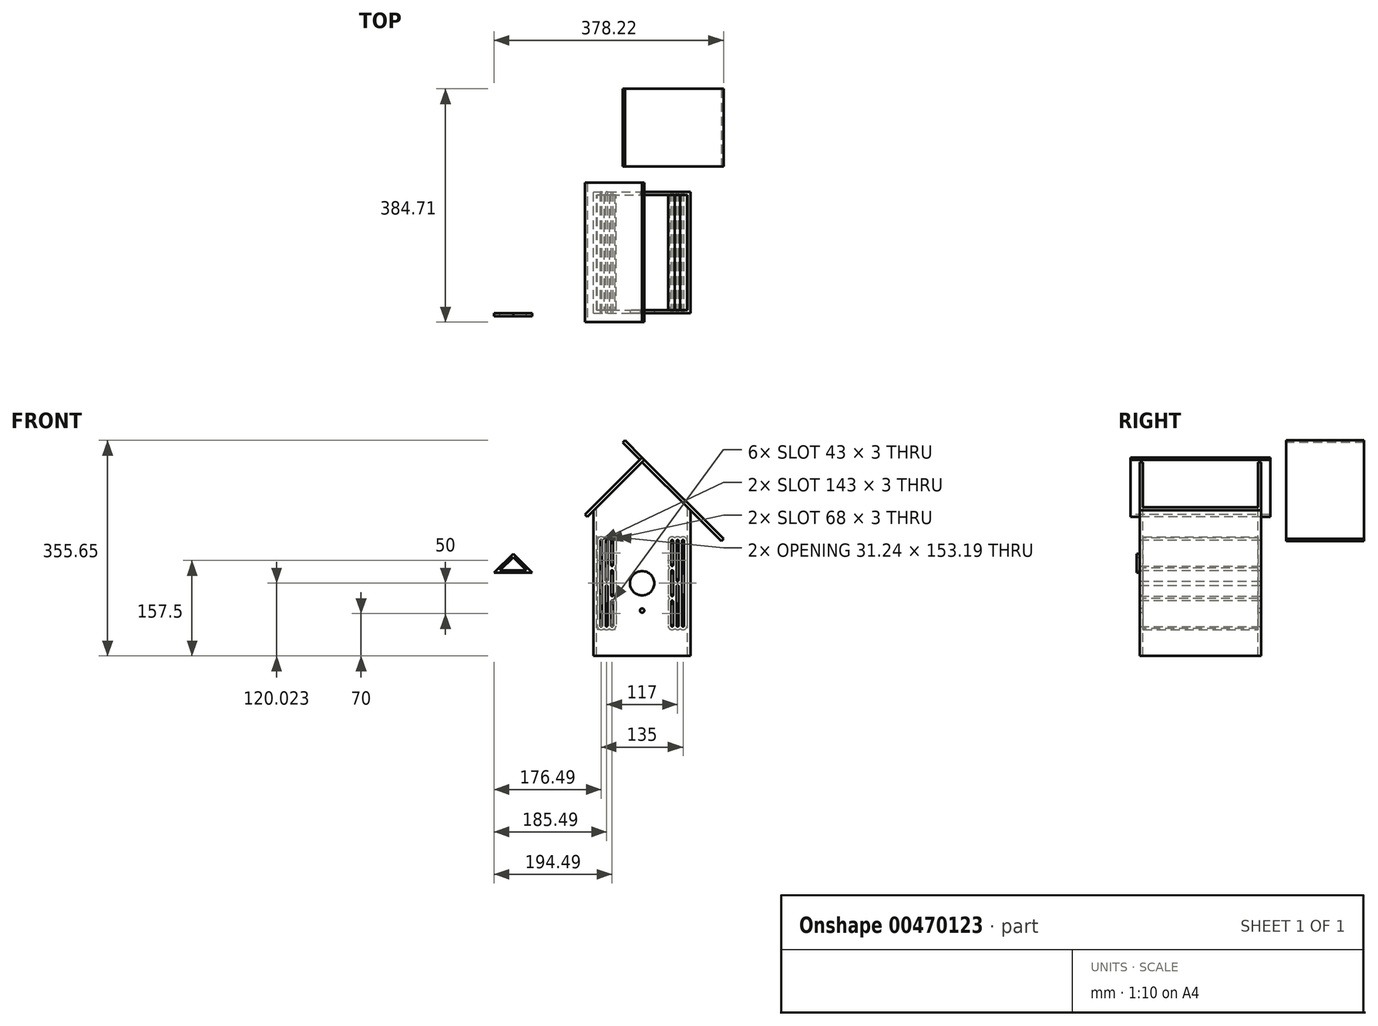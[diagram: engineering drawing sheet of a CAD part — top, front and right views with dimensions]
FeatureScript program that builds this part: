
annotation { "Feature Type Name" : "Feature", "Feature Type Description" : "" }
export const myFeature = defineFeature(function(context is Context, id is Id, definition is map)
    precondition{}
    {
        {
            var Q0;
            Q0=qCreatedBy(makeId("Front.planeOp"),FACE);
            var sketch = newSketch(context, id + "F0", { "sketchPlane" : qUnion([Q0])});
            skLineSegment(sketch, "E0.bottom", {"start": v(0, 0) * mm, "end": v(160, 0) * mm});
            skLineSegment(sketch, "E0.left", {"start": v(0, 0) * mm, "end": v(0, 240) * mm});
            skLineSegment(sketch, "E0.right", {"start": v(160, 0) * mm, "end": v(160, 240) * mm});
            skLineSegment(sketch, "E1", {"start": v(0, 240) * mm, "end": v(80, 320) * mm});
            skLineSegment(sketch, "E2", {"start": v(160, 240) * mm, "end": v(80, 320) * mm});
            skLineSegment(sketch, "E3", {"start": v(0, 240) * mm, "end": v(160, 240) * mm, "construction": true});
            skLineSegment(sketch, "E4.left", {"start": v(20, 190) * mm, "end": v(20, 125) * mm});
            skLineSegment(sketch, "E4.right", {"start": v(23, 190) * mm, "end": v(23, 125) * mm});
            skLineSegment(sketch, "E5", {"start": v(80, 249.53) * mm, "end": v(80, -21.44) * mm, "construction": true});
            skArc(sketch, "E6", {"start": v(23, 190) * mm, "mid": v(21.5, 191.5) * mm, "end": v(20, 190) * mm});
            skLineSegment(sketch, "E7", {"start": v(17, 266.29) * mm, "end": v(17, -25.67) * mm, "construction": true});
            skArc(sketch, "E8.MirrorCS", {"start": v(14, 50) * mm, "mid": v(12.5, 48.5) * mm, "end": v(11, 50) * mm});
            skArc(sketch, "E9.MirrorCS", {"start": v(11, 190) * mm, "mid": v(12.5, 191.5) * mm, "end": v(14, 190) * mm});
            skLineSegment(sketch, "E10.MirrorCS", {"start": v(11, 190) * mm, "end": v(11, 50) * mm});
            skLineSegment(sketch, "E11.MirrorCS", {"start": v(14, 190) * mm, "end": v(14, 50) * mm});
            skArc(sketch, "E12.MirrorCS", {"start": v(149, 190) * mm, "mid": v(147.5, 191.5) * mm, "end": v(146, 190) * mm});
            skArc(sketch, "E13.MirrorCS", {"start": v(146, 50) * mm, "mid": v(147.5, 48.5) * mm, "end": v(149, 50) * mm});
            skLineSegment(sketch, "E14.MirrorCS", {"start": v(149, 190) * mm, "end": v(149, 50) * mm});
            skLineSegment(sketch, "E15.MirrorCS", {"start": v(146, 190) * mm, "end": v(146, 50) * mm});
            skLineSegment(sketch, "E16.left", {"start": v(29, 190) * mm, "end": v(29, 150) * mm});
            skLineSegment(sketch, "E16.right", {"start": v(32, 190) * mm, "end": v(32, 150) * mm});
            skArc(sketch, "E17", {"start": v(29, 150) * mm, "mid": v(30.5, 148.5) * mm, "end": v(32, 150) * mm});
            skArc(sketch, "E18", {"start": v(32, 190) * mm, "mid": v(30.5, 191.5) * mm, "end": v(29, 190) * mm});
            skLineSegment(sketch, "E19.left", {"start": v(29, 140) * mm, "end": v(29, 100) * mm});
            skArc(sketch, "E20", {"start": v(32, 140) * mm, "mid": v(30.5, 141.5) * mm, "end": v(29, 140) * mm});
            skPoint(sketch, "E21.center.orphan", {"position": v(30.5, 70) * mm});
            skPoint(sketch, "E19.right.end.orphan", {"position": v(32, 40) * mm});
            skLineSegment(sketch, "E22", {"start": v(32, 140) * mm, "end": v(32, 100) * mm});
            skArc(sketch, "E23", {"start": v(29, 100) * mm, "mid": v(30.5, 98.5) * mm, "end": v(32, 100) * mm});
            skLineSegment(sketch, "E24", {"start": v(29, 90) * mm, "end": v(29, 50) * mm});
            skLineSegment(sketch, "E25", {"start": v(32, 90) * mm, "end": v(32, 50) * mm});
            skArc(sketch, "E26", {"start": v(29, 90) * mm, "mid": v(30.5, 91.5) * mm, "end": v(32, 90) * mm});
            skArc(sketch, "E27", {"start": v(29, 50) * mm, "mid": v(30.5, 48.5) * mm, "end": v(32, 50) * mm});
            skArc(sketch, "E28.MirrorCS", {"start": v(128, 190) * mm, "mid": v(129.5, 191.5) * mm, "end": v(131, 190) * mm});
            skArc(sketch, "E29.MirrorCS", {"start": v(128, 140) * mm, "mid": v(129.5, 141.5) * mm, "end": v(131, 140) * mm});
            skArc(sketch, "E30.MirrorCS", {"start": v(131, 150) * mm, "mid": v(129.5, 148.5) * mm, "end": v(128, 150) * mm});
            skArc(sketch, "E31.MirrorCS", {"start": v(131, 100) * mm, "mid": v(129.5, 98.5) * mm, "end": v(128, 100) * mm});
            skArc(sketch, "E32.MirrorCS", {"start": v(131, 90) * mm, "mid": v(129.5, 91.5) * mm, "end": v(128, 90) * mm});
            skArc(sketch, "E33.MirrorCS", {"start": v(131, 50) * mm, "mid": v(129.5, 48.5) * mm, "end": v(128, 50) * mm});
            skLineSegment(sketch, "E34.MirrorCS", {"start": v(131, 140) * mm, "end": v(131, 100) * mm});
            skLineSegment(sketch, "E35.MirrorCS", {"start": v(128, 90) * mm, "end": v(128, 50) * mm});
            skLineSegment(sketch, "E36.MirrorCS", {"start": v(131, 190) * mm, "end": v(131, 150) * mm});
            skLineSegment(sketch, "E37.MirrorCS", {"start": v(131, 90) * mm, "end": v(131, 50) * mm});
            skLineSegment(sketch, "E38.MirrorCS", {"start": v(128, 140) * mm, "end": v(128, 100) * mm});
            skLineSegment(sketch, "E39.MirrorCS", {"start": v(128, 190) * mm, "end": v(128, 150) * mm});
            skPoint(sketch, "E40.MirrorP", {"position": v(129.5, 70) * mm});
            skLineSegment(sketch, "E41", {"start": v(20.02, 115) * mm, "end": v(20.02, 50.05) * mm});
            skLineSegment(sketch, "E42", {"start": v(23.02, 115) * mm, "end": v(23.02, 50.05) * mm});
            skArc(sketch, "E43", {"start": v(23.02, 115) * mm, "mid": v(21.52, 116.5) * mm, "end": v(20.02, 115) * mm});
            skArc(sketch, "E44", {"start": v(20.02, 50.05) * mm, "mid": v(21.52, 48.55) * mm, "end": v(23.02, 50.05) * mm});
            skArc(sketch, "E45.MirrorCS", {"start": v(137, 190) * mm, "mid": v(138.5, 191.5) * mm, "end": v(140, 190) * mm});
            skArc(sketch, "E46.MirrorCS", {"start": v(136.98, 115) * mm, "mid": v(138.48, 116.5) * mm, "end": v(139.98, 115) * mm});
            skArc(sketch, "E47.MirrorCS", {"start": v(139.98, 50.05) * mm, "mid": v(138.48, 48.55) * mm, "end": v(136.98, 50.05) * mm});
            skLineSegment(sketch, "E48.MirrorCS", {"start": v(140, 190) * mm, "end": v(140, 125) * mm});
            skLineSegment(sketch, "E49.MirrorCS", {"start": v(139.98, 115) * mm, "end": v(139.98, 50.05) * mm});
            skLineSegment(sketch, "E50.MirrorCS", {"start": v(143, 266.29) * mm, "end": v(143, -25.67) * mm, "construction": true});
            skLineSegment(sketch, "E51.MirrorCS", {"start": v(137, 190) * mm, "end": v(137, 125) * mm});
            skLineSegment(sketch, "E52.MirrorCS", {"start": v(136.98, 115) * mm, "end": v(136.98, 50.05) * mm});
            skArc(sketch, "E53", {"start": v(20, 125) * mm, "mid": v(21.5, 123.5) * mm, "end": v(23, 125) * mm});
            skArc(sketch, "E54", {"start": v(137, 125) * mm, "mid": v(138.5, 123.5) * mm, "end": v(140, 125) * mm});
            skSolve(sketch);
        }
        {
            var Q0;
            Q0 = qSketchRegion(id + "F0", true);
            extrude(context, id + "F1", {"entities" : qUnion([Q0]), "offsetDistance" : 25 * mm, "depth" : 200 * mm});
        }
        {
            var Q0;
            Q0=makeQuery(id+"F1.opExtrude","SWEPT_FACE",FACE,{"disambiguationData":[OSD([sQuery(id+"F0.wireOp",EDGE,"E0.bottom")])]});
            var Q1;
            Q1=makeQuery(id+"F1.opExtrude","SWEPT_FACE",FACE,{"disambiguationData":[OSD([sQuery(id+"F0.wireOp",EDGE,"E2")])]});
            var Q2;
            Q2=makeQuery(id+"F1.opExtrude","SWEPT_FACE",FACE,{"disambiguationData":[OSD([sQuery(id+"F0.wireOp",EDGE,"E1")])]});
            shell(context, id + "F2", {"entities" : qUnion([Q0, Q1, Q2]), "thickness" : 5.12 * mm});
        }
        {
            var Q0;
            Q0=makeQuery(id+"F1.opExtrude","CAP_FACE",FACE,{"disambiguationData":[OSD([sQuery(id+"F0.wireOp",EDGE,"E0.bottom"),sQuery(id+"F0.wireOp",EDGE,"E0.left"),sQuery(id+"F0.wireOp",EDGE,"E0.right"),sQuery(id+"F0.wireOp",EDGE,"E1"),sQuery(id+"F0.wireOp",EDGE,"E2")])],"isStart":false});
            var sketch = newSketch(context, id + "F3", { "sketchPlane" : qUnion([Q0])});
            skLineSegment(sketch, "E55", {"start": v(80, 224.17) * mm, "end": v(80, 53.63) * mm, "construction": true});
            skLineSegment(sketch, "E56", {"start": v(0, 120) * mm, "end": v(241.44, 120) * mm, "construction": true});
            skLineSegment(sketch, "E57", {"start": v(17.26, 75) * mm, "end": v(140.48, 75) * mm, "construction": true});
            skCircle(sketch, "E58", {"center": v(80, 120) * mm, "radius": 20 * mm});
            skCircle(sketch, "E59", {"center": v(80, 75) * mm, "radius": 3.5 * mm});
            skSolve(sketch);
        }
        {
            var Q0;
            Q0=makeQuery(id+"F3.imprint","IMPRINT",FACE,{"disambiguationData":[TD([[makeQuery(id+"F3.imprint","IMPRINT",EDGE,{"derivedFrom":sQuery(id+"F3.wireOp",EDGE,"E58")}),1.0]])]});
            extrude(context, id + "F4", {"entities" : qUnion([Q0]), "operationType" : NewBodyOperationType.REMOVE, "oppositeDirection" : true, "depth" : 25 * mm, "offsetDistance" : 25 * mm});
        }
        {
            var Q0;
            Q0=makeQuery(id+"F3.imprint","IMPRINT",FACE,{"disambiguationData":[TD([[makeQuery(id+"F3.imprint","IMPRINT",EDGE,{"derivedFrom":sQuery(id+"F3.wireOp",EDGE,"E59")}),1.0]])]});
            var Q1;
            Q1=sQuery(id+"F3.wireOp",EDGE,"E59");
            extrude(context, id + "F5", {"entities" : qUnion([Q0]), "operationType" : NewBodyOperationType.REMOVE, "surfaceEntities" : qUnion([Q1]), "oppositeDirection" : true, "depth" : 220 * mm, "offsetDistance" : 25 * mm});
        }
        {
            var Q0;
            {var subQ0=sQuery(id+"F0.wireOp",EDGE,"E2");Q0=makeQuery(id+"F2.opShell","OFFSET_EDGE",EDGE,{"disambiguationData":[OSD([subQ0]),TDD([makeQuery(id+"F1.opExtrude","CAP_EDGE",EDGE,{"disambiguationData":[OSD([subQ0])],"isStart":false})])]});}
            var Q1;
            Q1=makeQuery(id+"F2.opShell","OFFSET_EDGE",EDGE,{"disambiguationData":[OSD([sQuery(id+"F0.wireOp",EDGE,"E0.right"),sQuery(id+"F0.wireOp",EDGE,"E2")])]});
            cPlane(context, id + "F6", {"entities" : qUnion([Q0, Q1]), "cplaneType" : CPlaneType.LINE_ANGLE, "offset" : 25 * mm, "angle" : 0 * degree, "width" : 150 * mm, "height" : 150 * mm});
        }
        {
            var Q0;
            Q0=qCreatedBy(id+"F6.planeOp",FACE);
            var sketch = newSketch(context, id + "F7", { "sketchPlane" : qUnion([Q0])});
            skLineSegment(sketch, "E60", {"start": v(-169.7, 215) * mm, "end": v(-41.57, 215) * mm});
            skLineSegment(sketch, "E61", {"start": v(-169.7, -15) * mm, "end": v(-41.57, -15) * mm});
            skLineSegment(sketch, "E62", {"start": v(-41.57, 215) * mm, "end": v(-41.57, -15) * mm});
            skLineSegment(sketch, "E63", {"start": v(-169.7, 215) * mm, "end": v(-169.7, -15) * mm});
            skSolve(sketch);
        }
        {
            var Q0;
            Q0 = qSketchRegion(id + "F7", true);
            extrude(context, id + "F8", {"entities" : qUnion([Q0]), "oppositeDirection" : true, "depth" : 5.12 * mm});
        }
        {
            var Q0;
            {var subQ0=sQuery(id+"F0.wireOp",EDGE,"E1");Q0=makeQuery(id+"F2.opShell","OFFSET_EDGE",EDGE,{"disambiguationData":[OSD([subQ0]),TDD([makeQuery(id+"F1.opExtrude","CAP_EDGE",EDGE,{"disambiguationData":[OSD([subQ0])],"isStart":false})])]});}
            var Q1;
            Q1=makeQuery(id+"F2.opShell","OFFSET_EDGE",EDGE,{"disambiguationData":[OSD([sQuery(id+"F0.wireOp",EDGE,"E0.left"),sQuery(id+"F0.wireOp",EDGE,"E1")])]});
            cPlane(context, id + "F9", {"entities" : qUnion([Q0, Q1]), "cplaneType" : CPlaneType.LINE_ANGLE, "offset" : 25 * mm, "angle" : 0 * degree, "width" : 150 * mm, "height" : 150 * mm});
        }
        {
            var Q0;
            Q0=qCreatedBy(id+"F9.planeOp",FACE);
            var sketch = newSketch(context, id + "F10", { "sketchPlane" : qUnion([Q0])});
            skLineSegment(sketch, "E64", {"start": v(-15, 287.96) * mm, "end": v(-15, 154.7) * mm});
            skLineSegment(sketch, "E65", {"start": v(215, 287.96) * mm, "end": v(215, 154.7) * mm});
            skLineSegment(sketch, "E66", {"start": v(-15, 287.96) * mm, "end": v(215, 287.96) * mm});
            skLineSegment(sketch, "E67", {"start": v(-15, 154.7) * mm, "end": v(215, 154.7) * mm});
            skSolve(sketch);
        }
        {
            var Q0;
            Q0 = qSketchRegion(id + "F10", true);
            extrude(context, id + "F11", {"entities" : qUnion([Q0]), "depth" : 5.12 * mm});
        }
        {
            var Q0;
            Q0=makeQuery(id+"F1.opExtrude","CAP_FACE",FACE,{"disambiguationData":[OSD([sQuery(id+"F0.wireOp",EDGE,"E0.bottom"),sQuery(id+"F0.wireOp",EDGE,"E0.left"),sQuery(id+"F0.wireOp",EDGE,"E0.right"),sQuery(id+"F0.wireOp",EDGE,"E1"),sQuery(id+"F0.wireOp",EDGE,"E2")])],"isStart":false});
            var sketch = newSketch(context, id + "F12", { "sketchPlane" : qUnion([Q0])});
            skLineSegment(sketch, "E68", {"start": v(8.16, 248.16) * mm, "end": v(80, 320) * mm});
            skLineSegment(sketch, "E69", {"start": v(8.16, 221.15) * mm, "end": v(80, 292.99) * mm});
            skLineSegment(sketch, "E70", {"start": v(8.16, 248.16) * mm, "end": v(8.16, 221.15) * mm});
            skLineSegment(sketch, "E71", {"start": v(80, 320) * mm, "end": v(151.84, 248.16) * mm});
            skLineSegment(sketch, "E72", {"start": v(80, 292.99) * mm, "end": v(151.84, 221.15) * mm});
            skLineSegment(sketch, "E73", {"start": v(151.84, 248.16) * mm, "end": v(151.84, 221.15) * mm});
            skLineSegment(sketch, "E74", {"start": v(80, 320) * mm, "end": v(80, 206.2) * mm, "construction": true});
            skLineSegment(sketch, "E75", {"start": v(80, 278.49) * mm, "end": v(14.88, 213.36) * mm});
            skLineSegment(sketch, "E76", {"start": v(80, 278.49) * mm, "end": v(145.12, 213.36) * mm});
            skLineSegment(sketch, "E77", {"start": v(80, 259.65) * mm, "end": v(14.88, 194.53) * mm});
            skLineSegment(sketch, "E78", {"start": v(14.88, 213.36) * mm, "end": v(14, 190) * mm});
            skLineSegment(sketch, "E79", {"start": v(145.12, 213.36) * mm, "end": v(145.12, 194.53) * mm});
            skLineSegment(sketch, "E80", {"start": v(80, 259.65) * mm, "end": v(145.12, 194.53) * mm});
            skPoint(sketch, "E81.orphan", {"position": v(146, 193.65) * mm});
            skSolve(sketch);
        }
        {
            var Q0;
            Q0=makeQuery(id+"F12.imprint","IMPRINT",FACE,{"disambiguationData":[TD([[makeQuery(id+"F12.imprint","IMPRINT",EDGE,{"derivedFrom":sQuery(id+"F12.wireOp",EDGE,"E69")}),-1.0]])]});
            var sketch = newSketch(context, id + "F13", { "sketchPlane" : qUnion([Q0])});
            skLineSegment(sketch, "E82", {"start": v(-164, 137.17) * mm, "end": v(-132.5, 168.67) * mm});
            skLineSegment(sketch, "E83", {"start": v(-101, 137.17) * mm, "end": v(-132.5, 168.67) * mm});
            skLineSegment(sketch, "E84", {"start": v(-164, 137.17) * mm, "end": v(-101, 137.17) * mm});
            skPoint(sketch, "E85.orphan", {"position": v(-38, 137.17) * mm});
            skLineSegment(sketch, "E86.0", {"start": v(-154.34, 141.17) * mm, "end": v(-132.5, 163.01) * mm});
            skLineSegment(sketch, "E86.1", {"start": v(-154.34, 141.17) * mm, "end": v(-110.66, 141.17) * mm});
            skLineSegment(sketch, "E86.2", {"start": v(-110.66, 141.17) * mm, "end": v(-132.5, 163.01) * mm});
            skSolve(sketch);
        }
        {
            var Q0;
            Q0 = qSketchRegion(id + "F13", true);
            extrude(context, id + "F14", {"entities" : qUnion([Q0]), "depth" : 5 * mm, "offsetDistance" : 25 * mm});
        }
    });
